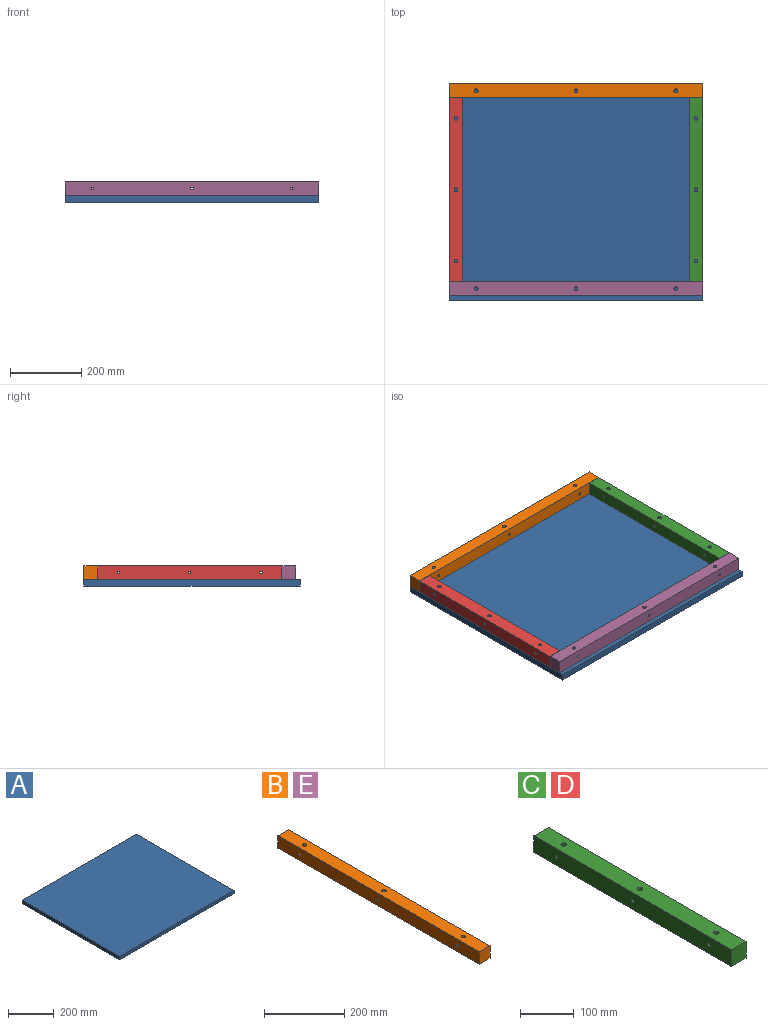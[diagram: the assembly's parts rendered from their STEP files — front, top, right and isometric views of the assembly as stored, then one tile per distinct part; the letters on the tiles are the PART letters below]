
ASSEMBLY  parts=5 mates=12
PART A: 6 faces, bbox 711.2x606.4x18.5 mm
  f0: plane 711.2x18.5mm, normal (0,-1,0), area 13157.2mm2, adj f1,f3,f4,f5
  f1: plane 606.43x18.5mm, normal (1,0,0), area 11218.9mm2, adj f0,f2,f4,f5
  f2: plane 711.2x18.5mm, normal (0,1,0), area 13157.2mm2, adj f1,f3,f4,f5
  f3: plane 606.43x18.5mm, normal (-1,0,0), area 11218.9mm2, adj f0,f2,f4,f5
  f4: plane 711.2x606.43mm, normal (0,0,1), area 431289.5mm2, adj f0,f1,f2,f3
  f5: plane 711.2x606.43mm, normal (0,0,-1), area 431289.5mm2, adj f0,f1,f2,f3
PART B: 15 faces, bbox 38.1x711.2x38.1 mm
  f0: cylinder r=5.16mm len=38.1mm, axis (0,0,1), area 1148.3mm2, adj f4,f6,f13,f14
  f1: cylinder r=5.16mm len=38.1mm, axis (0,0,1), area 1148.3mm2, adj f4,f6,f11,f12
  f2: cylinder r=5.16mm len=38.1mm, axis (0,0,1), area 1148.3mm2, adj f4,f6,f9,f10
  f3: plane 711.2x38.1mm, normal (1,0,0), area 26976.7mm2, adj f4,f6,f7,f8,f10,f12,f14
  f4: plane 711.2x38.1mm, normal (0,0,1), area 26846.1mm2, adj f0,f1,f2,f3,f5,f7,f8
  f5: plane 711.2x38.1mm, normal (-1,0,0), area 26976.7mm2, adj f4,f6,f7,f8,f9,f11,f13
  f6: plane 711.2x38.1mm, normal (0,0,-1), area 26846.1mm2, adj f0,f1,f2,f3,f5,f7,f8
  f7: plane 38.1x38.1mm, normal (0,-1,0), area 1451.6mm2, adj f3,f4,f5,f6
  f8: plane 38.1x38.1mm, normal (0,1,0), area 1451.6mm2, adj f3,f4,f5,f6
  f9: cylinder r=3.57mm len=15.33mm, axis (1,0,0), area 327mm2, adj f2,f5
  f10: cylinder r=3.57mm len=15.33mm, axis (1,0,0), area 327mm2, adj f2,f3
  f11: cylinder r=3.57mm len=15.33mm, axis (1,0,0), area 327mm2, adj f1,f5
  f12: cylinder r=3.57mm len=15.33mm, axis (1,0,0), area 327mm2, adj f1,f3
  f13: cylinder r=3.57mm len=15.33mm, axis (1,0,0), area 327mm2, adj f0,f5
  f14: cylinder r=3.57mm len=15.33mm, axis (1,0,0), area 327mm2, adj f0,f3
PART C: 15 faces, bbox 38.1x517.5x38.1 mm
  f0: cylinder r=5.16mm len=38.1mm, axis (0,0,1), area 1148.3mm2, adj f4,f6,f13,f14
  f1: cylinder r=5.16mm len=38.1mm, axis (0,0,1), area 1148.3mm2, adj f4,f6,f11,f12
  f2: cylinder r=5.16mm len=38.1mm, axis (0,0,1), area 1148.3mm2, adj f4,f6,f9,f10
  f3: plane 517.53x38.1mm, normal (1,0,0), area 19597.7mm2, adj f4,f6,f7,f8,f10,f12,f14
  f4: plane 517.53x38.1mm, normal (0,0,1), area 19467.1mm2, adj f0,f1,f2,f3,f5,f7,f8
  f5: plane 517.53x38.1mm, normal (-1,0,0), area 19597.7mm2, adj f4,f6,f7,f8,f9,f11,f13
  f6: plane 517.53x38.1mm, normal (0,0,-1), area 19467.1mm2, adj f0,f1,f2,f3,f5,f7,f8
  f7: plane 38.1x38.1mm, normal (0,-1,0), area 1451.6mm2, adj f3,f4,f5,f6
  f8: plane 38.1x38.1mm, normal (0,1,0), area 1451.6mm2, adj f3,f4,f5,f6
  f9: cylinder r=3.57mm len=15.33mm, axis (1,0,0), area 327mm2, adj f2,f5
  f10: cylinder r=3.57mm len=15.33mm, axis (1,0,0), area 327mm2, adj f2,f3
  f11: cylinder r=3.57mm len=15.33mm, axis (1,0,0), area 327mm2, adj f1,f5
  f12: cylinder r=3.57mm len=15.33mm, axis (1,0,0), area 327mm2, adj f1,f3
  f13: cylinder r=3.57mm len=15.33mm, axis (1,0,0), area 327mm2, adj f0,f5
  f14: cylinder r=3.57mm len=15.33mm, axis (1,0,0), area 327mm2, adj f0,f3
PART D: same geometry as C
PART E: same geometry as B
PLACE A t=(0,0,-18.5)mm
PLACE B rot(axis=(-0.71,-0.71,0),180deg) t=(355.6,284.16,19.05)mm
PLACE C t=(336.55,265.11,19.05)mm
PLACE D t=(-336.55,265.11,19.05)mm
PLACE E rot(axis=(0,0,1),90deg) t=(-355.6,-271.46,19.05)mm
MATE planar E.f7 <-> C.f11  axis (1,0,0) through (355.6,-271.46,19.05)mm
MATE planar B.f13 <-> C.f8  axis (0,-1,0) through (0,265.11,19.05)mm
MATE planar B.f0 <-> A.f4  axis (0,0,-1) through (0,284.16,0)mm
MATE planar E.f13 <-> C.f7  axis (0,1,0) through (0,-252.41,19.05)mm
MATE planar B.f8 <-> A.f1  axis (1,0,0) through (355.6,284.16,19.05)mm
MATE planar D.f8 <-> B.f13  axis (0,1,0) through (-336.55,265.11,19.05)mm
MATE planar D.f11 <-> B.f7  axis (-1,0,0) through (-355.6,6.35,19.05)mm
MATE planar C.f1 <-> A.f4  axis (0,0,-1) through (336.55,6.35,0)mm
MATE planar D.f1 <-> A.f4  axis (0,0,-1) through (-336.55,6.35,0)mm
MATE planar B.f13 <-> A.f2  axis (0,1,0) through (0,303.21,19.05)mm
MATE planar E.f0 <-> A.f4  axis (0,0,-1) through (0,-271.46,0)mm
MATE planar C.f11 <-> A.f1  axis (1,0,0) through (355.6,6.35,19.05)mm
